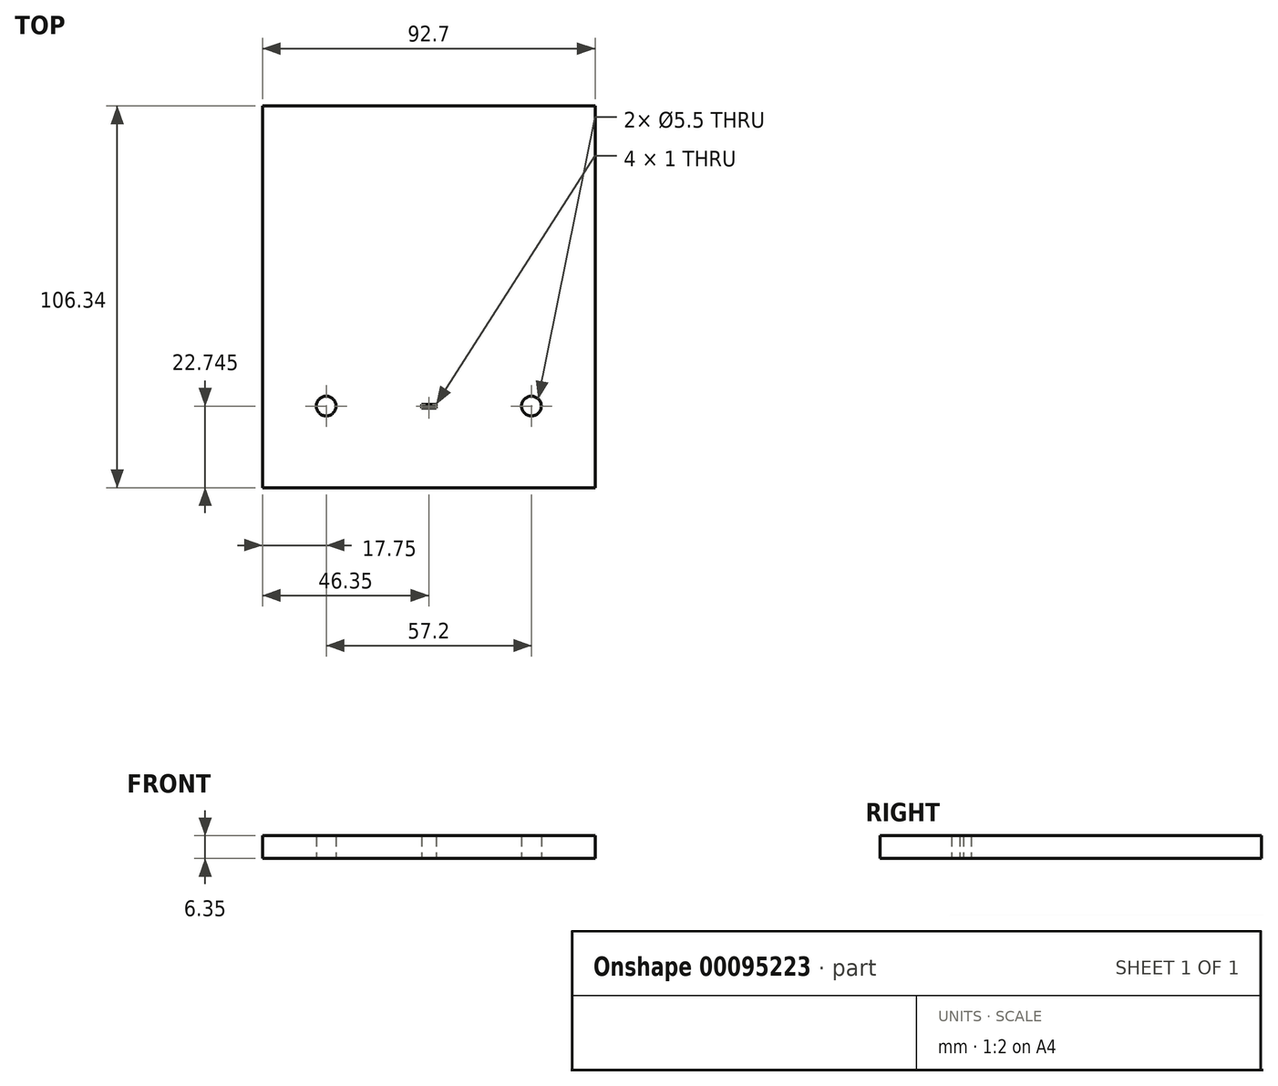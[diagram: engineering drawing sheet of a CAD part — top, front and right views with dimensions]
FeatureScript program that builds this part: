
annotation { "Feature Type Name" : "Feature", "Feature Type Description" : "" }
export const myFeature = defineFeature(function(context is Context, id is Id, definition is map)
    precondition{}
    {
        {
            var Q0;
            Q0=qCreatedBy(makeId("Top.planeOp"),FACE);
            var sketch = newSketch(context, id + "F0", { "sketchPlane" : qUnion([Q0])});
            skLineSegment(sketch, "E0.bottom", {"start": v(46.35, 53.17) * mm, "end": v(-46.35, 53.17) * mm});
            skLineSegment(sketch, "E0.top", {"start": v(46.35, -53.17) * mm, "end": v(-46.35, -53.17) * mm});
            skLineSegment(sketch, "E0.left", {"start": v(46.35, 53.17) * mm, "end": v(46.35, -53.17) * mm});
            skLineSegment(sketch, "E0.right", {"start": v(-46.35, 53.17) * mm, "end": v(-46.35, -53.17) * mm});
            skPoint(sketch, "E0.middle", {"position": v(0, 0) * mm});
            skCircle(sketch, "E1", {"center": v(28.6, -30.42) * mm, "radius": 2.75 * mm});
            skLineSegment(sketch, "E2", {"start": v(28.6, -33.17) * mm, "end": v(28.6, -53.17) * mm, "construction": true});
            skLineSegment(sketch, "E3", {"start": v(31.35, -30.42) * mm, "end": v(46.35, -30.42) * mm, "construction": true});
            skLineSegment(sketch, "E4", {"start": v(28.6, -33.17) * mm, "end": v(28.6, -30.42) * mm, "construction": true});
            skLineSegment(sketch, "E5", {"start": v(31.35, -30.42) * mm, "end": v(28.6, -30.42) * mm, "construction": true});
            skCircle(sketch, "E6.MirrorC", {"center": v(-28.6, -30.42) * mm, "radius": 2.75 * mm});
            skPoint(sketch, "E7.orphan", {"position": v(4.1, -29.92) * mm});
            skPoint(sketch, "E8.center.orphan", {"position": v(0, -30.43) * mm});
            skPoint(sketch, "E8.start.orphan", {"position": v(-0.67, -29.92) * mm});
            skPoint(sketch, "E9.start.orphan", {"position": v(1.71, -29.92) * mm});
            skLineSegment(sketch, "E10.bottom", {"start": v(2, -29.92) * mm, "end": v(-2, -29.92) * mm});
            skLineSegment(sketch, "E10.top", {"start": v(2, -30.92) * mm, "end": v(-2, -30.92) * mm});
            skLineSegment(sketch, "E10.left", {"start": v(2, -29.92) * mm, "end": v(2, -30.92) * mm});
            skLineSegment(sketch, "E10.right", {"start": v(-2, -29.92) * mm, "end": v(-2, -30.92) * mm});
            skSolve(sketch);
        }
        {
            var Q0;
            Q0=makeQuery(id+"F0.imprint","IMPRINT",FACE,{"disambiguationData":[TD([[makeQuery(id+"F0.imprint","IMPRINT",EDGE,{"derivedFrom":sQuery(id+"F0.wireOp",EDGE,"E0.bottom")}),1.0]])]});
            extrude(context, id + "F1", {"entities" : qUnion([Q0]), "depth" : 6.35 * mm});
        }
    });
